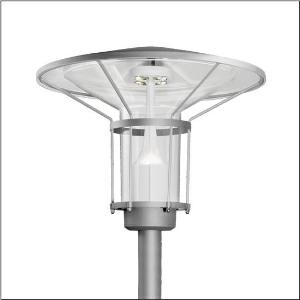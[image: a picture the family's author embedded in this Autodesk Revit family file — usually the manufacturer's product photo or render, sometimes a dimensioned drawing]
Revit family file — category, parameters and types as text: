
# Revit family: laterne_classic___st1_2a_5xa5243ab14h_e952
name_source: partatom
category: Lighting Fixtures
units: mm (PartAtom-declared; Revit-internal decimal feet)

## family parameters
Cut with Voids When Loaded = No
Host = Face
Light Source = No
Part Type = Normal
Room Calculation Point = No
Round Connector Dimension = Use Diameter
Shared = No

## types (1)
- --- (1 x LED, 1380 lm, 14.9 W, 2200K)
    Apparent Load = 15 VA
    CIE Flux Codes = 21 60 93 97 100
    Color Rendering = 70
    Color Temperature = 2200K
    Default Elevation = 1800 mm
    Description = Lantern Classic, mast luminaire, Module 540 Plus, primary light control with 3 zone facetted reflector, of plastic, silver coated, highly specular, structured, primary optical cover: cover, of PMMA, transparent, light distribution: ST1.2a, light emission: direct distribution, primary light characteristic: asymmetric, installation type: post-top, LED, High Power LED, rated luminous flux: 1.380lm, luminous efficacy: 93lm/W, light colour: 722, colour temperature: 2200K, control gear: ECG Plus, control: flexible luminous flux parameterisation, time-dependent luminous flux control, digital communication interface, power reduction, overheat protection, constant luminous flux control, electronic power reduction, with terminal, 6-pole, max. 2.5mm², mains connection: 230..240V, AC, 50/60Hz, start of lifetime: 15W, end of service life: 16W, reduction: 7W, luminaire housing, upper part, of glass-fibre reinforced polyester, coated, Siteco® metallic grey (DB 702S), diameter: 750mm, height: 596mm, spigot size: d x l = 76 x 70mm (post-top) | with reducer (optional accessory) 60 x 70mm, post-top mast mounting element, of diecast aluminium, coated, Siteco® metallic grey (DB 702S), Module 540 Plus, traffic white (RAL 9016), equipment: standard, protection rating (complete): IP65, insulation class (complete): insulation class II (safety insulation), certification: CE, ENEC, VDE, packaging unit: 1 piece

Light Distribution: ST1.2a
    Height = 596 mm
    Lamp = 1 x LED
    Lamp Light Flux = 1380 lm
    Lamp Power = 14.9 W
    Lamp count = 1
    Length = 750 mm
    Luminous efficacy = 93 lm/W
    Manufacturer = Siteco
    ModVariant = No
    Model = 5XA5243AB14H
    Number of Poles = 1
    OnlyDefault = Yes
    Power Factor = 1
    Product Name = Laterne Classic | ST1.2a
    Product group = mast luminaire | pylon top
    ProductGroupID = 6100
    Protection Class = Protection class II
    Protection Degree = IP 65
    RLX_Detail_Level = 1
    RLX_Emergency_Light_Flux = 0 lm
    RLX_Emergency_Type = 0
    RLX_Emergency_Type_DB = No
    RlxData = <blob elided: 92921 chars, md5=63614189>
    Socket = socket
    Standby Power = 0 W
    System Light Flux = 1380 lm
    System Power = 15 W
    Type Comments = factory setting: luminous flux: 100 % | dim-lin: 254 | 570 mA
    Type Image = l_1006052.jpg
    URL = http://relux.com
    VarID = @adj_139976
    Voltage = 0 V
    Weight = 0.00 kg
    Width = 0 mm  [stored 0 ft]

note: [stored X ft] marks values corroborated as IEEE doubles in the binary element streams (Revit-internal decimal feet)

## geometry (parser evidence)
native form markers: Blend x4, Sweep x9
no freeform markers — native parametric forms only
